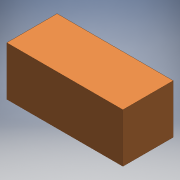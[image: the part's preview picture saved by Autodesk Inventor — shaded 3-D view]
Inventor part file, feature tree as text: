
AUTODESK INVENTOR PART (.ipt)
format: ipt  version: 2016 (Build 200138000, 138)  size: 104,960 bytes
history: native  units: mm
features: extrude x2, sketch x2, other x1
ambient origin geometry x8: Origin, YZ Plane, XZ Plane, XY Plane, X Axis, Y Axis, Z Axis, Center Point
bodies: Body1 (feature_tree)
feature tree (5):
  other  "Sólido1"
  extrude  "Extrusión1"  Depth=19.0mm TaperAngle=0.0deg
  extrude  "Extrusión2"  [1 undecoded]
  sketch  "Boceto1"  dims[d7=19.5mm d8=0.0mm d17=19.0mm d18=0.0mm]
  sketch  "Boceto2"
note: 1 required parameter value undecoded (feature->parameter linkage not recoverable at this tier; creation-order binding heuristic only, values carry confidence <= 0.55)
